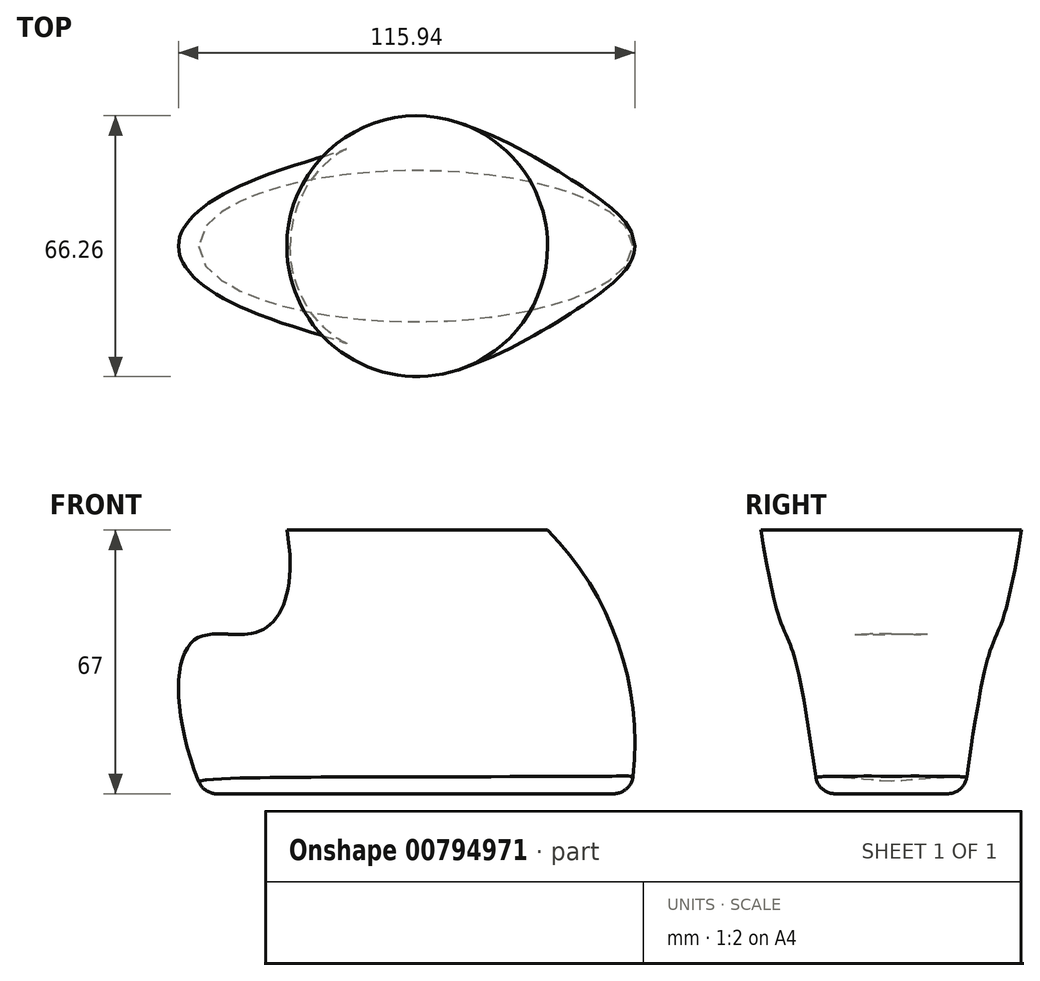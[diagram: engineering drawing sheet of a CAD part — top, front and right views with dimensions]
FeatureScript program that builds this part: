
annotation { "Feature Type Name" : "Feature", "Feature Type Description" : "" }
export const myFeature = defineFeature(function(context is Context, id is Id, definition is map)
    precondition{}
    {
        {
            var Q0;
            Q0=qCreatedBy(makeId("Top.planeOp"),FACE);
            var sketch = newSketch(context, id + "F0", { "sketchPlane" : qUnion([Q0])});
            skEllipse(sketch, "E0", {"center": v(0, 0) * mm, "majorRadius": 54.24 * mm, "minorRadius": 18.58 * mm, "majorAxis": v(1, 0)});
            skLineSegment(sketch, "E1", {"start": v(-54.24, 0) * mm, "end": v(54.24, 0) * mm});
            skSolve(sketch);
        }
        {
            var Q0;
            Q0=qCreatedBy(makeId("Top.planeOp"),FACE);
            cPlane(context, id + "F1", {"entities" : qUnion([Q0]), "cplaneType" : CPlaneType.OFFSET, "offset" : 67 * mm, "width" : 150 * mm, "height" : 150 * mm});
        }
        {
            var Q0;
            Q0=qCreatedBy(id+"F1.planeOp",FACE);
            var sketch = newSketch(context, id + "F2", { "sketchPlane" : qUnion([Q0])});
            skCircle(sketch, "E2", {"center": v(0, 0) * mm, "radius": 33.13 * mm});
            skLineSegment(sketch, "E3", {"start": v(-33.13, 0) * mm, "end": v(33.13, 0) * mm});
            skSolve(sketch);
        }
        {
            var Q0;
            Q0=qCreatedBy(makeId("Front.planeOp"),FACE);
            var sketch = newSketch(context, id + "F3", { "sketchPlane" : qUnion([Q0])});
            skFitSpline(sketch, "E4", {"points": [v(-54.24, 0) * mm, v(-56.23, 39.34) * mm, v(-40.67, 41.07) * mm, v(-33.13, 67) * mm], "startDerivative": vector(-58.9, 135.14) * mm, "endDerivative": vector(-23.47, 128.66) * mm});
            skSolve(sketch);
        }
        {
            var Q0;
            Q0=qCreatedBy(makeId("Front.planeOp"),FACE);
            var sketch = newSketch(context, id + "F4", { "sketchPlane" : qUnion([Q0])});
            skArc(sketch, "E5", {"start": v(54.24, 0) * mm, "mid": v(51.73, 36.04) * mm, "end": v(33.13, 67) * mm});
            skSolve(sketch);
        }
        {
            var Q0;
            {var subQ0=sQuery(id+"F2.wireOp",EDGE,"E3");Q0=makeQuery(id+"F2.imprint","IMPRINT",FACE,{"disambiguationData":[TD([[makeQuery(id+"F2.imprint","IMPRINT",EDGE,{"derivedFrom":subQ0}),-1.0]])]});}
            var Q1;
            {var subQ0=sQuery(id+"F0.wireOp",EDGE,"E1");Q1=makeQuery(id+"F0.imprint","IMPRINT",FACE,{"disambiguationData":[TD([[makeQuery(id+"F0.imprint","IMPRINT",EDGE,{"derivedFrom":subQ0}),-1.0]])]});}
            var Q2;
            Q2=sQuery(id+"F3.wireOp",EDGE,"E4");
            var Q3;
            Q3=sQuery(id+"F4.wireOp",EDGE,"E5");
            loft(context, id + "F5", {"addGuides" : true, "sheetProfilesArray" : [{ "sheetProfileEntities" : qUnion([Q0]) }, { "sheetProfileEntities" : qUnion([Q1]) }], "guidesArray" : [{ "guideEntities" : qUnion([Q2]), "guideDerivativeType" : LoftGuideDerivativeType.DEFAULT, "guideDerivativeMagnitude" : 1 }, { "guideEntities" : qUnion([Q3]), "guideDerivativeType" : LoftGuideDerivativeType.DEFAULT, "guideDerivativeMagnitude" : 1 }]});
        }
        {
            var Q0;
            {var subQ0=sQuery(id+"F2.wireOp",EDGE,"E3");var subQ2=sQuery(id+"F0.wireOp",EDGE,"E1");Q0=makeQuery(id+"F5.opLoft","SWEPT_BODY",BODY,{"disambiguationData":[OSD([makeQuery(id+"F0.imprint","IMPRINT",FACE,{"disambiguationData":[TD([[makeQuery(id+"F0.imprint","IMPRINT",EDGE,{"derivedFrom":subQ2}),-1.0]])]}),makeQuery(id+"F2.imprint","IMPRINT",FACE,{"disambiguationData":[TD([[makeQuery(id+"F2.imprint","IMPRINT",EDGE,{"derivedFrom":subQ0}),-1.0]])]}),sQuery(id+"F3.wireOp",EDGE,"E4"),sQuery(id+"F4.wireOp",EDGE,"E5")])]});}
            var Q1;
            Q1=qCreatedBy(makeId("Front.planeOp"),FACE);
            mirror(context, id + "F6", {"operationType" : NewBodyOperationType.ADD, "entities" : qUnion([Q0]), "mirrorPlane" : qUnion([Q1])});
        }
        {
            var Q0;
            {var subQ0=sQuery(id+"F0.wireOp",EDGE,"E1");var subQ1=sQuery(id+"F0.wireOp",EDGE,"E0");var subQ2=makeQuery(id+"F0.imprint","INTERSECT",VERTEX,{"disambiguationData":[OD(0.0)],"derivedFrom":[subQ1,subQ0]});var subQ3=makeQuery(id+"F0.imprint","INTERSECT",VERTEX,{"disambiguationData":[OD(1.0)],"derivedFrom":[subQ1,subQ0]});Q0=makeQuery(id+"F6.opPattern","COPY",EDGE,{"derivedFrom":makeQuery(id+"F5.opLoft","MID_CAP_EDGE",EDGE,{"disambiguationData":[OSD([subQ1,subQ0]),TDD([subQ2,subQ3,makeQuery(id+"F0.imprint","IMPRINT",EDGE,{"disambiguationData":[TD([[subQ2,-1.0]])],"derivedFrom":subQ1})])],"capPos":1.0}),"instanceName":"1"});}
            fillet(context, id + "F7", {"entities" : qUnion([Q0]), "radius" : 5 * mm, "tangentPropagation" : true, "allowEdgeOverflow" : false});
        }
    });
